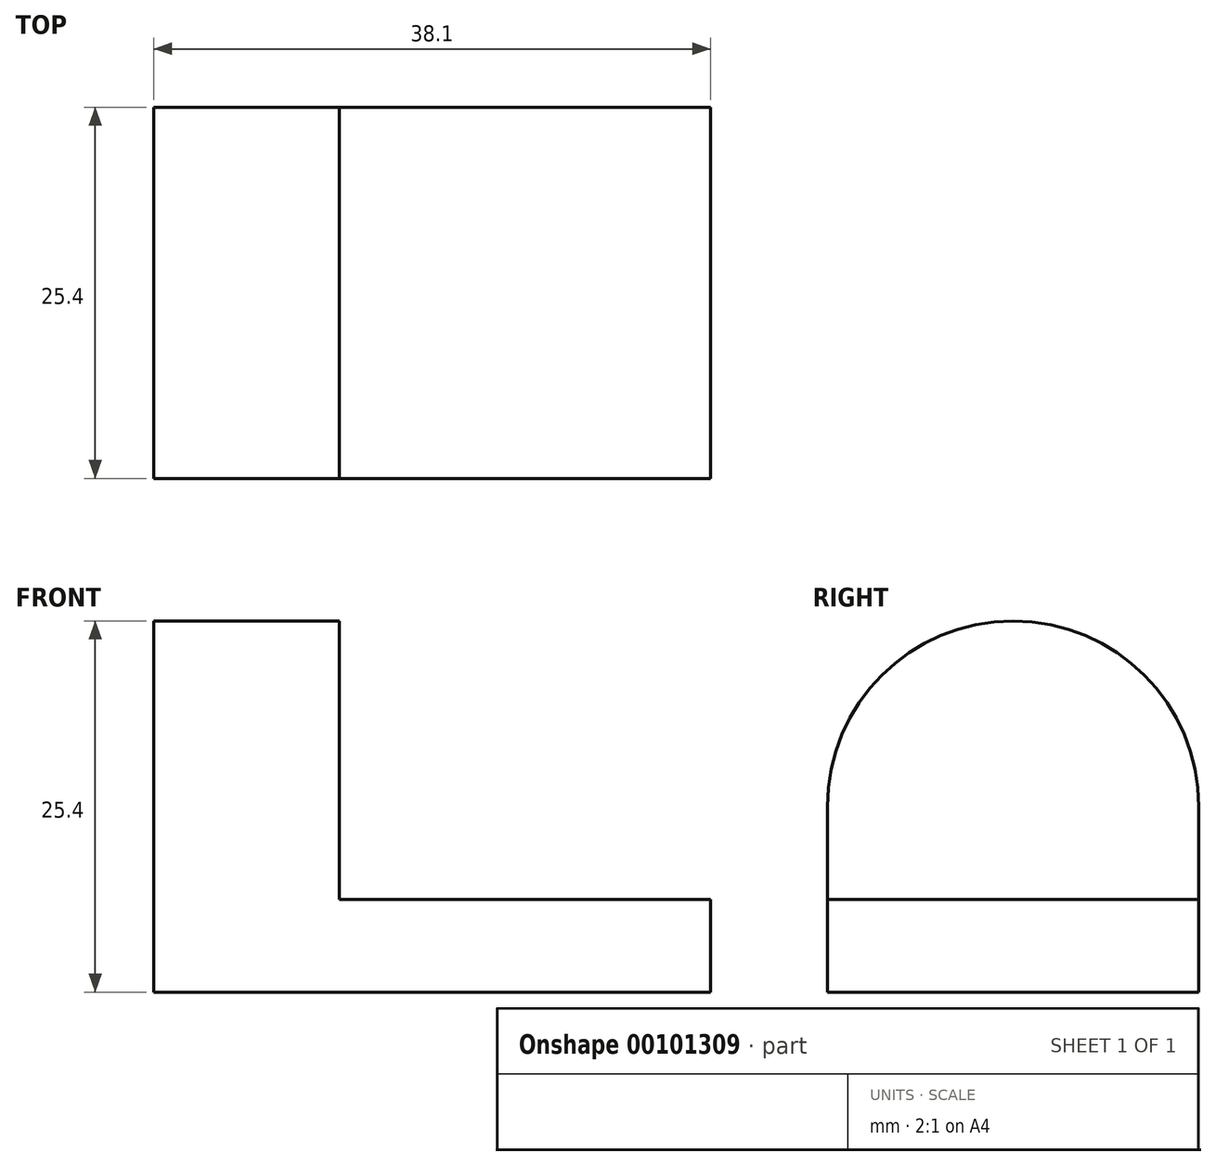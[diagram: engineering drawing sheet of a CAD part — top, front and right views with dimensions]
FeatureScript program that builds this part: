
annotation { "Feature Type Name" : "Feature", "Feature Type Description" : "" }
export const myFeature = defineFeature(function(context is Context, id is Id, definition is map)
    precondition{}
    {
        {
            var Q0;
            Q0=qCreatedBy(makeId("Front.planeOp"),FACE);
            var sketch = newSketch(context, id + "F0", { "sketchPlane" : qUnion([Q0])});
            skLineSegment(sketch, "E0", {"start": v(0, 0) * mm, "end": v(-38.1, 0) * mm});
            skLineSegment(sketch, "E1", {"start": v(-38.1, 0) * mm, "end": v(-38.1, 6.35) * mm});
            skLineSegment(sketch, "E2", {"start": v(-38.1, 6.35) * mm, "end": v(0, 6.35) * mm});
            skLineSegment(sketch, "E3", {"start": v(0, 6.35) * mm, "end": v(0, 0) * mm});
            skSolve(sketch);
        }
        {
            var Q0;
            Q0 = qSketchRegion(id + "F0", true);
            extrude(context, id + "F1", {"entities" : qUnion([Q0]), "oppositeDirection" : true, "depth" : 25.4 * mm});
        }
        {
            var Q0;
            Q0=makeQuery(id+"F1.opExtrude","SWEPT_FACE",FACE,{"disambiguationData":[OSD([sQuery(id+"F0.wireOp",EDGE,"E1")])]});
            var sketch = newSketch(context, id + "F2", { "sketchPlane" : qUnion([Q0])});
            skLineSegment(sketch, "E4", {"start": v(0, 12.7) * mm, "end": v(0, 0) * mm});
            skLineSegment(sketch, "E5", {"start": v(0, 0) * mm, "end": v(-25.4, 0) * mm});
            skLineSegment(sketch, "E6", {"start": v(-25.4, 0) * mm, "end": v(-25.4, 12.7) * mm});
            skArc(sketch, "E7", {"start": v(0, 12.7) * mm, "mid": v(-12.7, 25.4) * mm, "end": v(-25.4, 12.7) * mm});
            skSolve(sketch);
        }
        {
            var Q0;
            Q0 = qSketchRegion(id + "F2", true);
            extrude(context, id + "F3", {"entities" : qUnion([Q0]), "operationType" : NewBodyOperationType.ADD, "oppositeDirection" : true, "depth" : 12.7 * mm});
        }
    });
